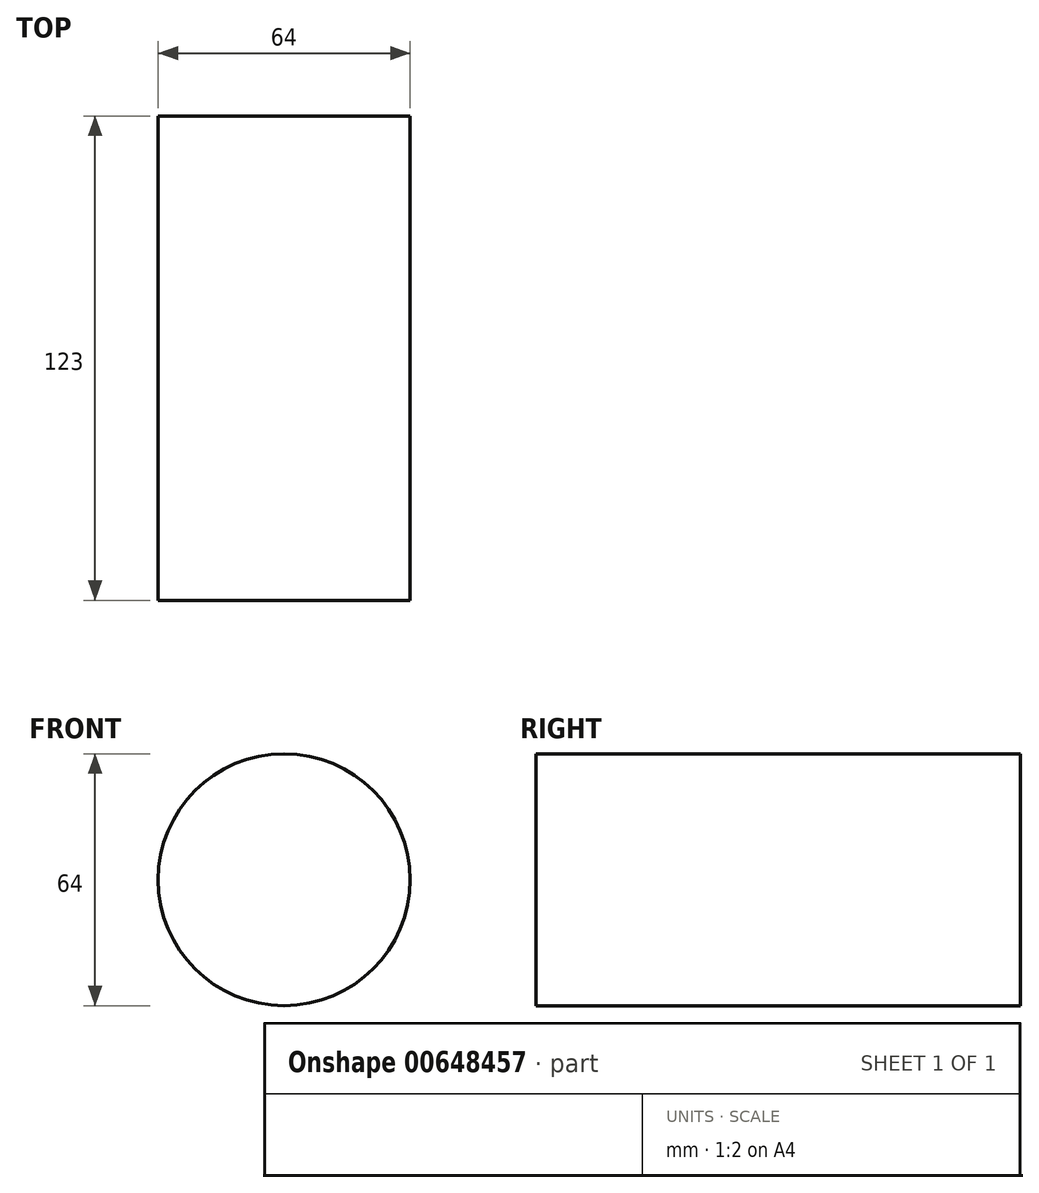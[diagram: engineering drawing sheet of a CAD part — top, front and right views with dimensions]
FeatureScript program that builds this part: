
annotation { "Feature Type Name" : "Feature", "Feature Type Description" : "" }
export const myFeature = defineFeature(function(context is Context, id is Id, definition is map)
    precondition{}
    {
        {
            var Q0;
            Q0=qCreatedBy(makeId("Front.planeOp"),FACE);
            var sketch = newSketch(context, id + "F0", { "sketchPlane" : qUnion([Q0])});
            skCircle(sketch, "E0", {"center": v(0, 0) * mm, "radius": 32 * mm});
            skSolve(sketch);
        }
        {
            var Q0;
            Q0 = qSketchRegion(id + "F0", true);
            var Q1;
            Q1=makeQuery(id+"F0.imprint","IMPRINT",FACE,{"disambiguationData":[TD([[makeQuery(id+"F0.imprint","IMPRINT",EDGE,{"derivedFrom":sQuery(id+"F0.wireOp",EDGE,"E0")}),1.0]])]});
            extrude(context, id + "F1", {"entities" : qUnion([Q0, Q1]), "depth" : 123 * mm, "offsetDistance" : 25 * mm});
        }
    });
